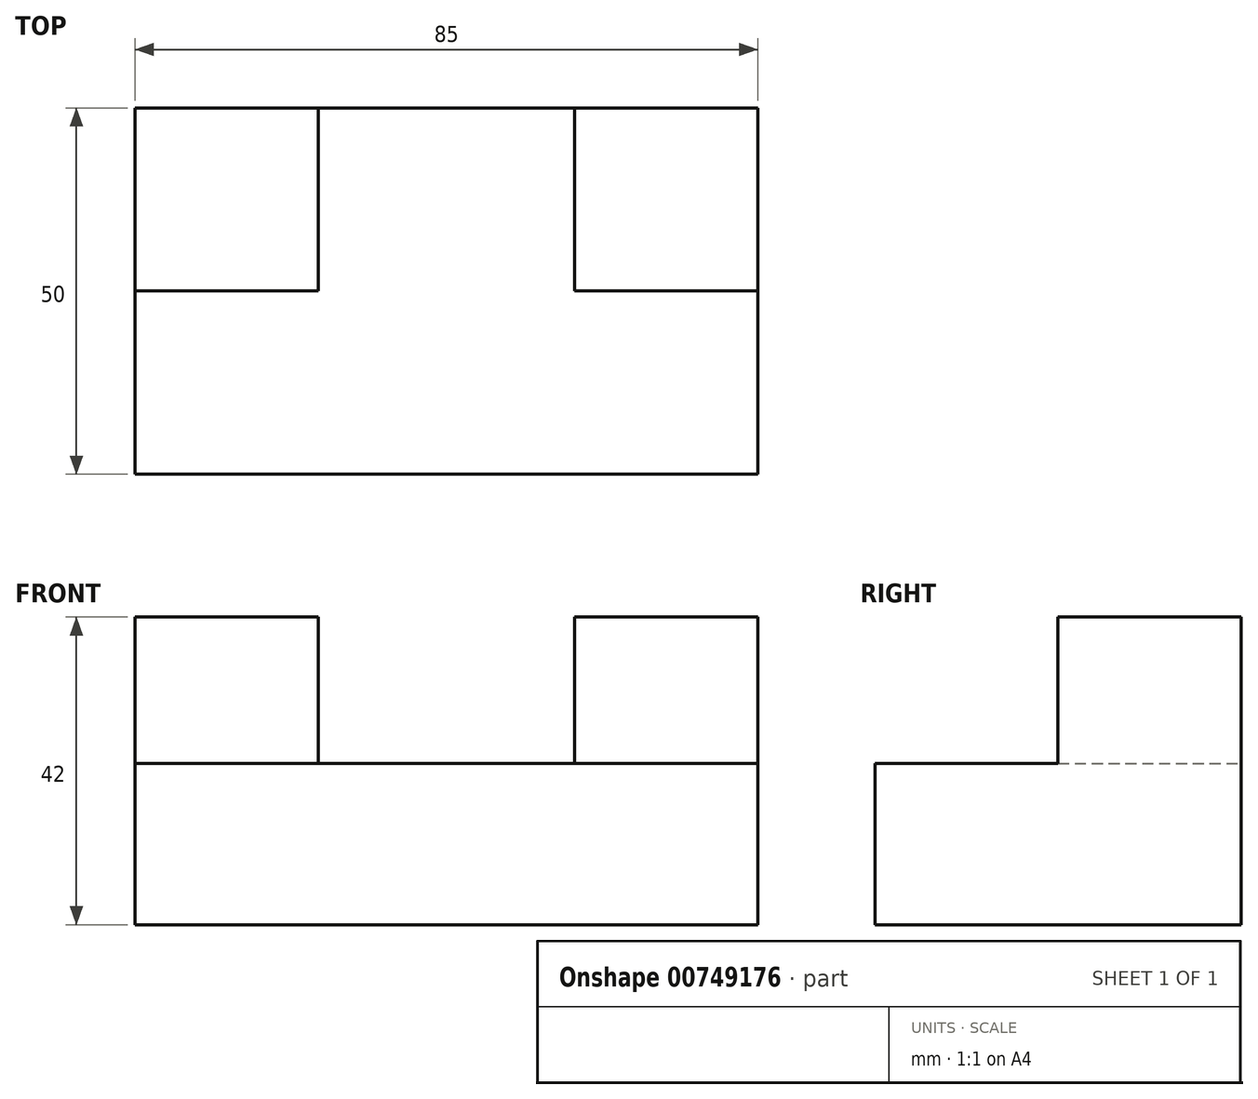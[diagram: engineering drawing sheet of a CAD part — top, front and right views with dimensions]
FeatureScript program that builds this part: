
annotation { "Feature Type Name" : "Feature", "Feature Type Description" : "" }
export const myFeature = defineFeature(function(context is Context, id is Id, definition is map)
    precondition{}
    {
        {
            var Q0;
            Q0=qCreatedBy(makeId("Top.planeOp"),FACE);
            var sketch = newSketch(context, id + "F0", { "sketchPlane" : qUnion([Q0])});
            skLineSegment(sketch, "E0.bottom", {"start": v(0, 50) * mm, "end": v(85, 50) * mm});
            skLineSegment(sketch, "E0.top", {"start": v(0, 0) * mm, "end": v(85, 0) * mm});
            skLineSegment(sketch, "E0.left", {"start": v(0, 50) * mm, "end": v(0, 0) * mm});
            skLineSegment(sketch, "E0.right", {"start": v(85, 50) * mm, "end": v(85, 0) * mm});
            skLineSegment(sketch, "E1.bottom", {"start": v(85, 25) * mm, "end": v(60, 25) * mm});
            skLineSegment(sketch, "E1.top", {"start": v(85, 50) * mm, "end": v(60, 50) * mm});
            skLineSegment(sketch, "E1.left", {"start": v(85, 25) * mm, "end": v(85, 50) * mm});
            skLineSegment(sketch, "E1.right", {"start": v(60, 25) * mm, "end": v(60, 50) * mm});
            skLineSegment(sketch, "E2.bottom", {"start": v(0, 50) * mm, "end": v(25, 50) * mm});
            skLineSegment(sketch, "E2.top", {"start": v(0, 25) * mm, "end": v(25, 25) * mm});
            skLineSegment(sketch, "E2.left", {"start": v(0, 50) * mm, "end": v(0, 25) * mm});
            skLineSegment(sketch, "E2.right", {"start": v(25, 50) * mm, "end": v(25, 25) * mm});
            skSolve(sketch);
        }
        {
            var Q0;
            {var subQ1=sQuery(id+"F0.wireOp",EDGE,"E0.top");Q0=makeQuery(id+"F0.imprint","IMPRINT",FACE,{"disambiguationData":[TD([[makeQuery(id+"F0.imprint","IMPRINT",EDGE,{"derivedFrom":subQ1}),1.0]])]});}
            extrude(context, id + "F1", {"entities" : qUnion([Q0]), "depth" : 22 * mm, "offsetDistance" : 25 * mm});
        }
        {
            var Q0;
            {var subQ4=sQuery(id+"F0.wireOp",EDGE,"E2.top");Q0=makeQuery(id+"F0.imprint","IMPRINT",FACE,{"disambiguationData":[TD([[makeQuery(id+"F0.imprint","IMPRINT",EDGE,{"derivedFrom":subQ4}),1.0]])]});}
            var Q1;
            {var subQ4=sQuery(id+"F0.wireOp",EDGE,"E1.bottom");Q1=makeQuery(id+"F0.imprint","IMPRINT",FACE,{"disambiguationData":[TD([[makeQuery(id+"F0.imprint","IMPRINT",EDGE,{"derivedFrom":subQ4}),-1.0]])]});}
            extrude(context, id + "F2", {"entities" : qUnion([Q0, Q1]), "operationType" : NewBodyOperationType.ADD, "depth" : 42 * mm, "offsetDistance" : 25 * mm});
        }
    });
